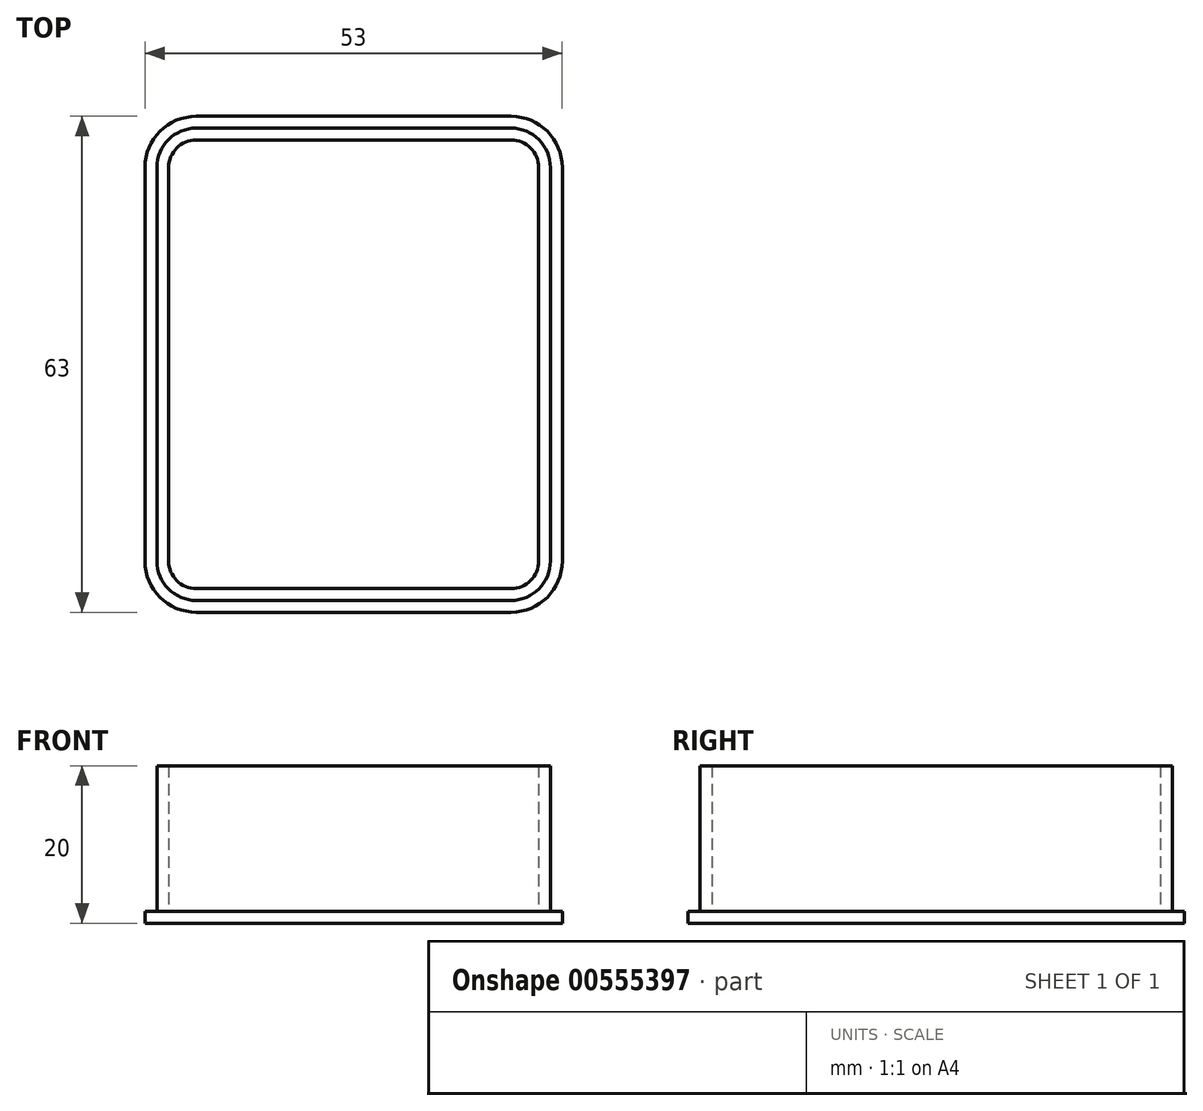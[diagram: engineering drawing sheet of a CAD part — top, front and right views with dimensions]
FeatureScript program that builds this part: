
annotation { "Feature Type Name" : "Feature", "Feature Type Description" : "" }
export const myFeature = defineFeature(function(context is Context, id is Id, definition is map)
    precondition{}
    {
        {
            var Q0;
            Q0=qCreatedBy(makeId("Top.planeOp"),FACE);
            var sketch = newSketch(context, id + "F0", { "sketchPlane" : qUnion([Q0])});
            skLineSegment(sketch, "E0.bottom", {"start": v(20.5, 30) * mm, "end": v(-19.5, 30) * mm});
            skLineSegment(sketch, "E0.top", {"start": v(20.5, -30) * mm, "end": v(-19.5, -30) * mm});
            skLineSegment(sketch, "E0.left", {"start": v(25.5, 25) * mm, "end": v(25.5, -25) * mm});
            skLineSegment(sketch, "E0.right", {"start": v(-24.5, 25) * mm, "end": v(-24.5, -25) * mm});
            skPoint(sketch, "E1.visualSharp", {"position": v(-24.5, 30) * mm});
            skArc(sketch, "E1.filletArc", {"start": v(-19.5, 30) * mm, "mid": v(-23.03, 28.54) * mm, "end": v(-24.5, 25) * mm});
            skPoint(sketch, "E2.visualSharp", {"position": v(25.5, 30) * mm});
            skArc(sketch, "E2.filletArc", {"start": v(25.5, 25) * mm, "mid": v(24.04, 28.54) * mm, "end": v(20.5, 30) * mm});
            skPoint(sketch, "E3.visualSharp", {"position": v(-24.5, -30) * mm});
            skArc(sketch, "E3.filletArc", {"start": v(-24.5, -25) * mm, "mid": v(-23.03, -28.54) * mm, "end": v(-19.5, -30) * mm});
            skPoint(sketch, "E4.visualSharp", {"position": v(25.5, -30) * mm});
            skArc(sketch, "E4.filletArc", {"start": v(20.5, -30) * mm, "mid": v(24.04, -28.54) * mm, "end": v(25.5, -25) * mm});
            skLineSegment(sketch, "E5.0", {"start": v(-26, 25) * mm, "end": v(-26, -25) * mm});
            skArc(sketch, "E6.0", {"start": v(-19.5, 31.5) * mm, "mid": v(-24.1, 29.6) * mm, "end": v(-26, 25) * mm});
            skLineSegment(sketch, "E6.1", {"start": v(20.5, 31.5) * mm, "end": v(-19.5, 31.5) * mm});
            skArc(sketch, "E6.2", {"start": v(27, 25) * mm, "mid": v(25.1, 29.6) * mm, "end": v(20.5, 31.5) * mm});
            skArc(sketch, "E6.3", {"start": v(-26, -25) * mm, "mid": v(-24.1, -29.6) * mm, "end": v(-19.5, -31.5) * mm});
            skLineSegment(sketch, "E6.4", {"start": v(20.5, -31.5) * mm, "end": v(-19.5, -31.5) * mm});
            skArc(sketch, "E6.5", {"start": v(20.5, -31.5) * mm, "mid": v(25.1, -29.6) * mm, "end": v(27, -25) * mm});
            skLineSegment(sketch, "E6.6", {"start": v(27, 25) * mm, "end": v(27, -25) * mm});
            skArc(sketch, "E7.0", {"start": v(24, 25) * mm, "mid": v(22.98, 27.47) * mm, "end": v(20.5, 28.5) * mm});
            skLineSegment(sketch, "E7.1", {"start": v(20.5, 28.5) * mm, "end": v(-19.5, 28.5) * mm});
            skLineSegment(sketch, "E7.2", {"start": v(24, 25) * mm, "end": v(24, -25) * mm});
            skArc(sketch, "E7.3", {"start": v(-19.5, 28.5) * mm, "mid": v(-21.97, 27.47) * mm, "end": v(-23, 25) * mm});
            skArc(sketch, "E7.4", {"start": v(20.5, -28.5) * mm, "mid": v(22.98, -27.47) * mm, "end": v(24, -25) * mm});
            skLineSegment(sketch, "E7.5", {"start": v(20.5, -28.5) * mm, "end": v(-19.5, -28.5) * mm});
            skArc(sketch, "E7.6", {"start": v(-23, -25) * mm, "mid": v(-21.97, -27.47) * mm, "end": v(-19.5, -28.5) * mm});
            skLineSegment(sketch, "E7.7", {"start": v(-23, 25) * mm, "end": v(-23, -25) * mm});
            skSolve(sketch);
        }
        {
            var Q0;
            Q0=makeQuery(id+"F0.imprint","IMPRINT",FACE,{"disambiguationData":[TD([[makeQuery(id+"F0.imprint","IMPRINT",EDGE,{"derivedFrom":sQuery(id+"F0.wireOp",EDGE,"E0.bottom")}),-1.0]])]});
            var Q1;
            Q1=makeQuery(id+"F0.imprint","IMPRINT",FACE,{"disambiguationData":[TD([[makeQuery(id+"F0.imprint","IMPRINT",EDGE,{"derivedFrom":sQuery(id+"F0.wireOp",EDGE,"E0.bottom")}),1.0]])]});
            var Q2;
            Q2=makeQuery(id+"F0.imprint","IMPRINT",FACE,{"disambiguationData":[TD([[makeQuery(id+"F0.imprint","IMPRINT",EDGE,{"derivedFrom":sQuery(id+"F0.wireOp",EDGE,"E7.0")}),1.0]])]});
            extrude(context, id + "F1", {"entities" : qUnion([Q0, Q1, Q2]), "depth" : 1.5 * mm, "offsetDistance" : 25 * mm});
        }
        {
            var Q0;
            Q0=makeQuery(id+"F0.imprint","IMPRINT",FACE,{"disambiguationData":[TD([[makeQuery(id+"F0.imprint","IMPRINT",EDGE,{"derivedFrom":sQuery(id+"F0.wireOp",EDGE,"E0.bottom")}),1.0]])]});
            extrude(context, id + "F2", {"entities" : qUnion([Q0]), "operationType" : NewBodyOperationType.ADD, "depth" : 20 * mm, "offsetDistance" : 25 * mm});
        }
    });
